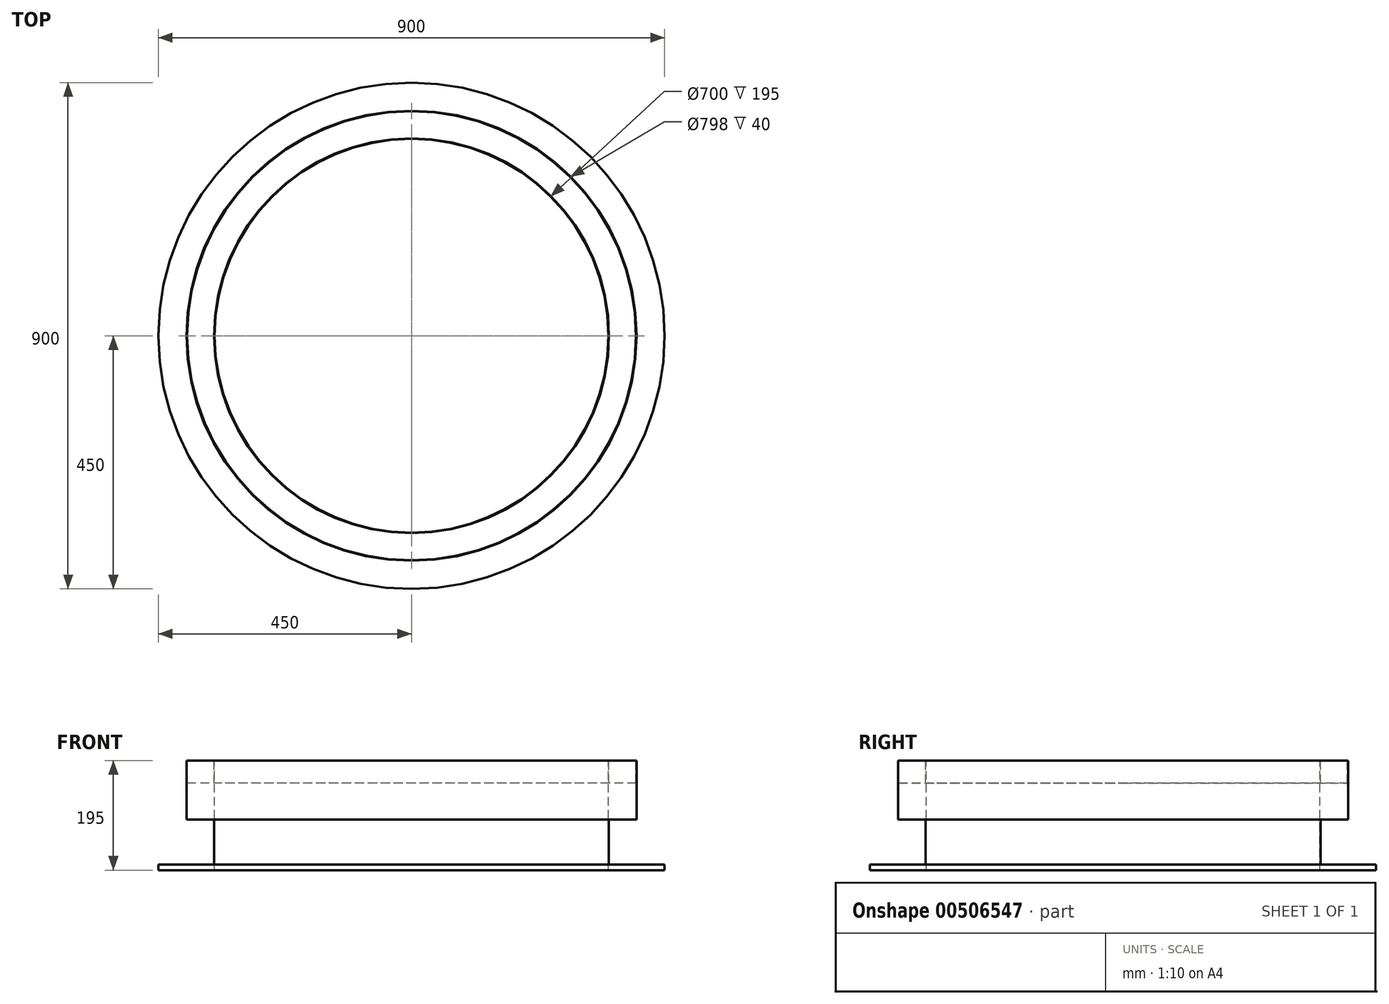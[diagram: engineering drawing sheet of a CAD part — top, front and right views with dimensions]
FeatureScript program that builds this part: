
annotation { "Feature Type Name" : "Feature", "Feature Type Description" : "" }
export const myFeature = defineFeature(function(context is Context, id is Id, definition is map)
    precondition{}
    {
        {
            var Q0;
            Q0=qCreatedBy(makeId("Front.planeOp"),FACE);
            var sketch = newSketch(context, id + "F0", { "sketchPlane" : qUnion([Q0])});
            skLineSegment(sketch, "E0", {"start": v(0, 710.75) * mm, "end": v(0, -704.58) * mm, "construction": true});
            skLineSegment(sketch, "E1", {"start": v(-350, 300.65) * mm, "end": v(-350, 495.65) * mm});
            skLineSegment(sketch, "E2", {"start": v(-350, 495.65) * mm, "end": v(-351, 495.65) * mm});
            skLineSegment(sketch, "E3", {"start": v(-399, 495.65) * mm, "end": v(-400, 495.65) * mm});
            skLineSegment(sketch, "E4", {"start": v(-400, 495.65) * mm, "end": v(-400, 390.65) * mm});
            skLineSegment(sketch, "E5", {"start": v(-400, 390.65) * mm, "end": v(-351, 390.65) * mm});
            skLineSegment(sketch, "E6", {"start": v(-351, 390.65) * mm, "end": v(-351, 310.65) * mm});
            skLineSegment(sketch, "E7", {"start": v(-351, 310.65) * mm, "end": v(-450, 310.65) * mm});
            skLineSegment(sketch, "E8", {"start": v(-450, 310.65) * mm, "end": v(-450, 300.65) * mm});
            skLineSegment(sketch, "E9", {"start": v(-450, 300.65) * mm, "end": v(-350, 300.65) * mm});
            skLineSegment(sketch, "E10", {"start": v(-399, 495.65) * mm, "end": v(-399, 455.65) * mm});
            skLineSegment(sketch, "E11", {"start": v(-399, 455.65) * mm, "end": v(-351, 455.65) * mm});
            skLineSegment(sketch, "E12", {"start": v(-351, 455.65) * mm, "end": v(-351, 495.65) * mm});
            skSolve(sketch);
        }
        {
            var Q0;
            Q0=qSketchRegion(id+"F0",true);
            var Q1;
            Q1=sQuery(id+"F0.wireOp",EDGE,"E0");
            revolve(context, id + "F1", {"entities" : qUnion([Q0]), "axis" : qUnion([Q1]), "revolveType" : RevolveType.FULL});
        }
    });
